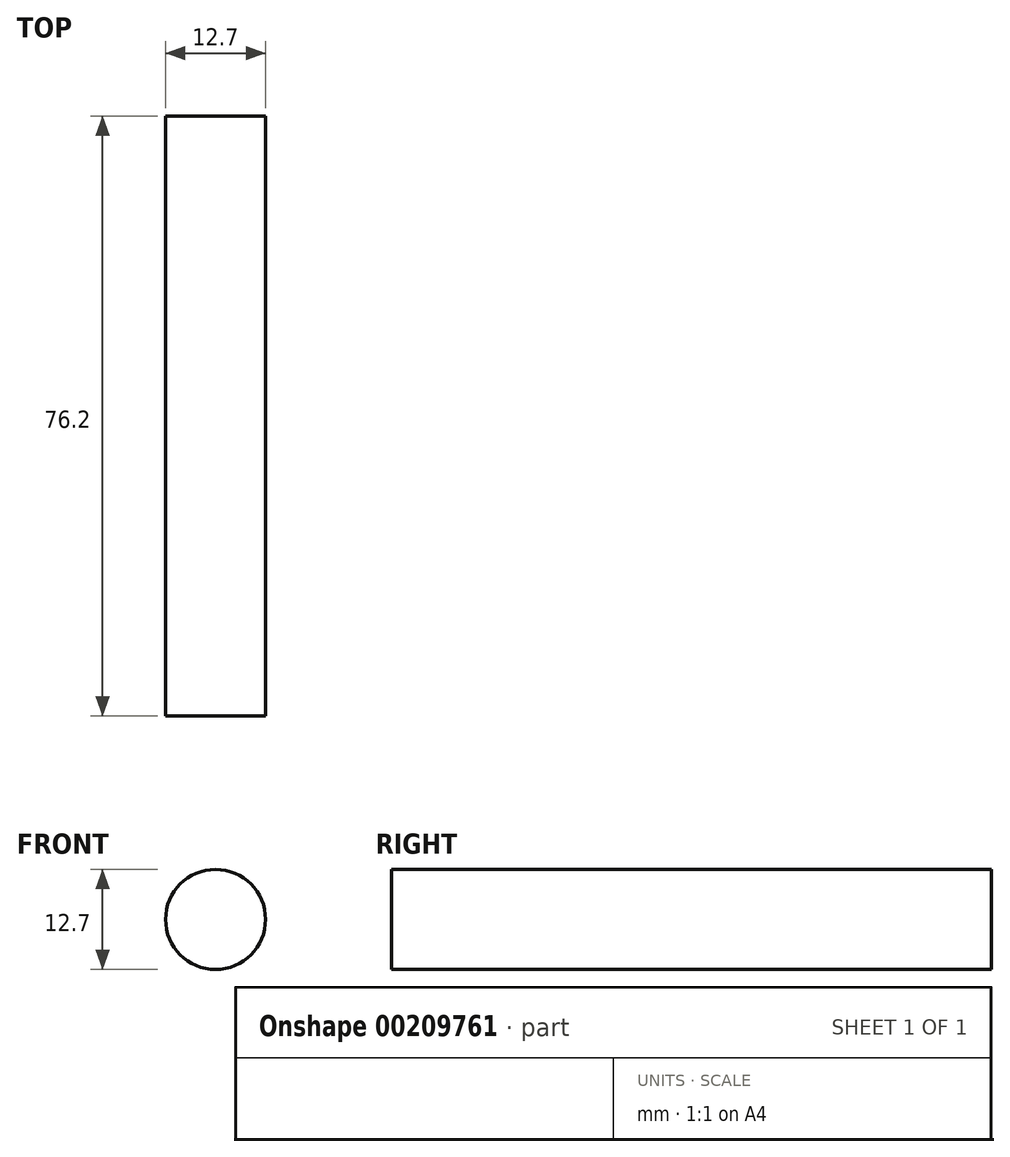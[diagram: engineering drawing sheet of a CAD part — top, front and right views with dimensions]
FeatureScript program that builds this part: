
annotation { "Feature Type Name" : "Feature", "Feature Type Description" : "" }
export const myFeature = defineFeature(function(context is Context, id is Id, definition is map)
    precondition{}
    {
        {
            var Q0;
            Q0=qCreatedBy(makeId("Top.planeOp"),FACE);
            var sketch = newSketch(context, id + "F0", { "sketchPlane" : qUnion([Q0])});
            skLineSegment(sketch, "E0.bottom", {"start": v(0, 0) * mm, "end": v(6.35, 0) * mm});
            skLineSegment(sketch, "E0.top", {"start": v(0, 76.2) * mm, "end": v(6.35, 76.2) * mm});
            skLineSegment(sketch, "E0.left", {"start": v(0, 0) * mm, "end": v(0, 76.2) * mm});
            skLineSegment(sketch, "E0.right", {"start": v(6.35, 0) * mm, "end": v(6.35, 76.2) * mm});
            skLineSegment(sketch, "E1", {"start": v(0, 0) * mm, "end": v(0, 85.4) * mm});
            skSolve(sketch);
        }
        {
            var Q0;
            Q0 = qSketchRegion(id + "F0", true);
            var Q1;
            Q1=sQuery(id+"F0.wireOp",EDGE,"E1");
            revolve(context, id + "F1", {"entities" : qUnion([Q0]), "axis" : qUnion([Q1]), "revolveType" : RevolveType.FULL});
        }
    });
